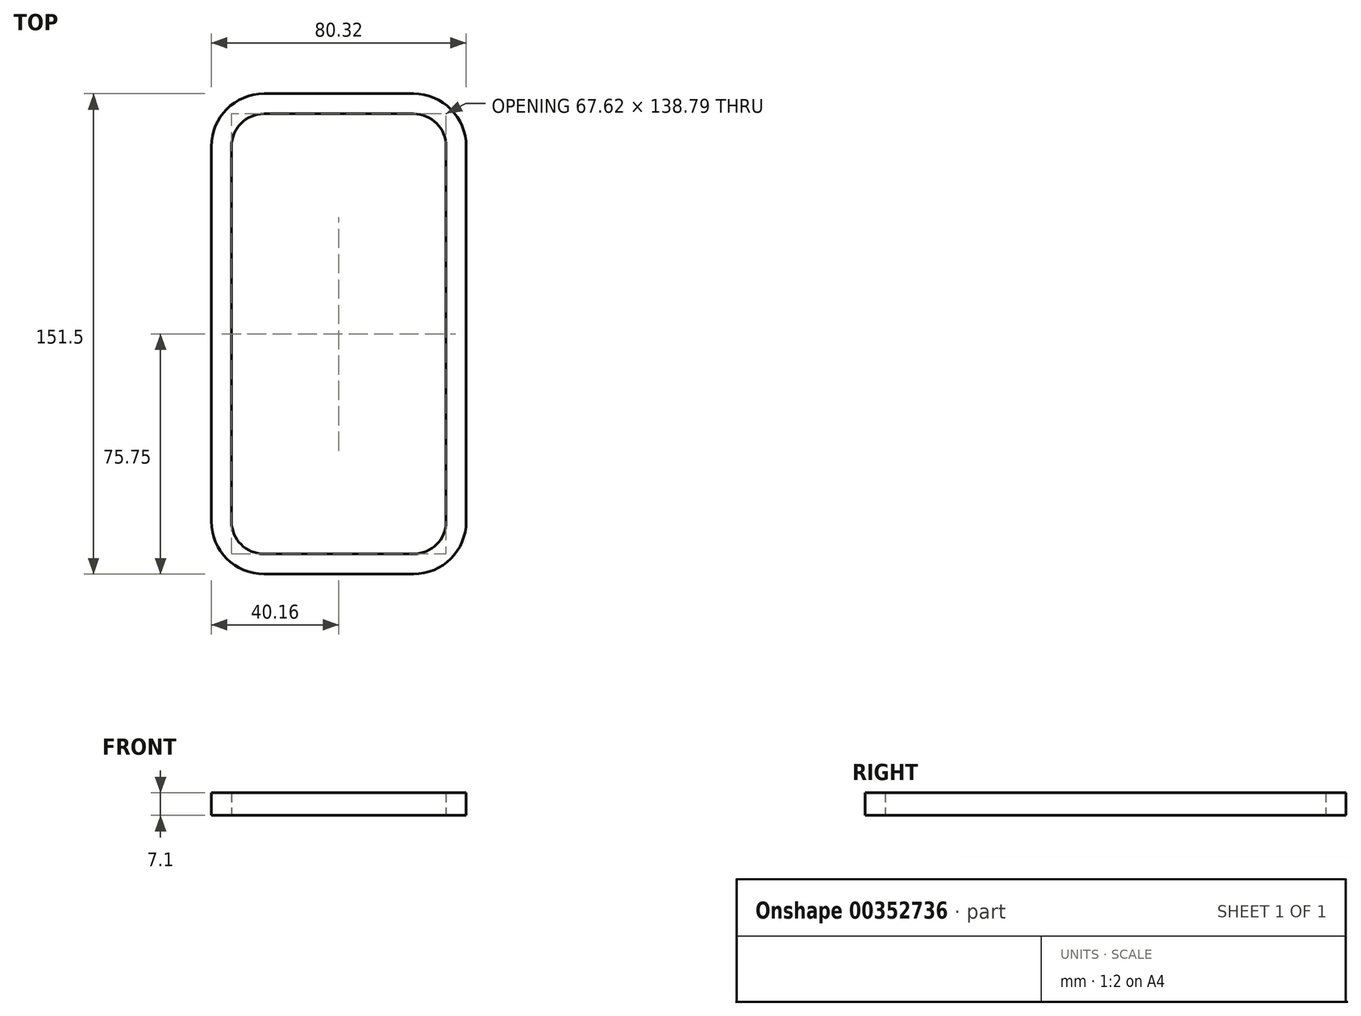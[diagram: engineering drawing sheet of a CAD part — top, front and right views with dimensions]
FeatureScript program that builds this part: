
annotation { "Feature Type Name" : "Feature", "Feature Type Description" : "" }
export const myFeature = defineFeature(function(context is Context, id is Id, definition is map)
    precondition{}
    {
        {
            var Q0;
            Q0=qCreatedBy(makeId("Top.planeOp"),FACE);
            var sketch = newSketch(context, id + "F0", { "sketchPlane" : qUnion([Q0])});
            skPoint(sketch, "E0.middle", {"position": v(0, 0) * mm});
            skPoint(sketch, "E1.visualSharp", {"position": v(-33.56, 69.14) * mm});
            skPoint(sketch, "E2.visualSharp", {"position": v(33.56, 69.14) * mm});
            skPoint(sketch, "E3.visualSharp", {"position": v(-33.56, -69.14) * mm});
            skPoint(sketch, "E4.visualSharp", {"position": v(33.56, -69.14) * mm});
            skArc(sketch, "E5.0", {"start": v(23.56, -69.4) * mm, "mid": v(30.8, -66.4) * mm, "end": v(33.81, -59.14) * mm});
            skLineSegment(sketch, "E5.1", {"start": v(23.56, -69.4) * mm, "end": v(-23.56, -69.4) * mm});
            skLineSegment(sketch, "E5.2", {"start": v(33.81, -59.14) * mm, "end": v(33.81, 59.14) * mm});
            skArc(sketch, "E5.3", {"start": v(-33.8, -59.14) * mm, "mid": v(-30.8, -66.4) * mm, "end": v(-23.56, -69.4) * mm});
            skArc(sketch, "E5.4", {"start": v(33.81, 59.14) * mm, "mid": v(30.8, 66.4) * mm, "end": v(23.56, 69.4) * mm});
            skLineSegment(sketch, "E5.5", {"start": v(23.56, 69.4) * mm, "end": v(-23.56, 69.4) * mm});
            skArc(sketch, "E5.6", {"start": v(-23.56, 69.4) * mm, "mid": v(-30.8, 66.4) * mm, "end": v(-33.8, 59.14) * mm});
            skLineSegment(sketch, "E5.7", {"start": v(-33.8, -59.14) * mm, "end": v(-33.8, 59.14) * mm});
            skArc(sketch, "E6.0", {"start": v(23.56, -75.74) * mm, "mid": v(35.3, -70.88) * mm, "end": v(40.16, -59.14) * mm});
            skLineSegment(sketch, "E6.1", {"start": v(23.56, -75.74) * mm, "end": v(-23.56, -75.74) * mm});
            skLineSegment(sketch, "E6.2", {"start": v(40.16, -59.14) * mm, "end": v(40.16, 59.14) * mm});
            skArc(sketch, "E6.3", {"start": v(-40.16, -59.14) * mm, "mid": v(-35.3, -70.88) * mm, "end": v(-23.56, -75.74) * mm});
            skArc(sketch, "E6.4", {"start": v(40.16, 59.14) * mm, "mid": v(35.3, 70.88) * mm, "end": v(23.56, 75.75) * mm});
            skLineSegment(sketch, "E6.5", {"start": v(23.56, 75.74) * mm, "end": v(-23.56, 75.74) * mm});
            skArc(sketch, "E6.6", {"start": v(-23.56, 75.74) * mm, "mid": v(-35.3, 70.88) * mm, "end": v(-40.16, 59.14) * mm});
            skLineSegment(sketch, "E6.7", {"start": v(-40.16, -59.14) * mm, "end": v(-40.16, 59.14) * mm});
            skSolve(sketch);
        }
        {
            var Q0;
            Q0=makeQuery(id+"F0.imprint","IMPRINT",FACE,{"disambiguationData":[TD([[makeQuery(id+"F0.imprint","IMPRINT",EDGE,{"derivedFrom":sQuery(id+"F0.wireOp",EDGE,"E5.0")}),-1.0]])]});
            extrude(context, id + "F1", {"entities" : qUnion([Q0]), "depth" : 7.1 * mm});
        }
    });
